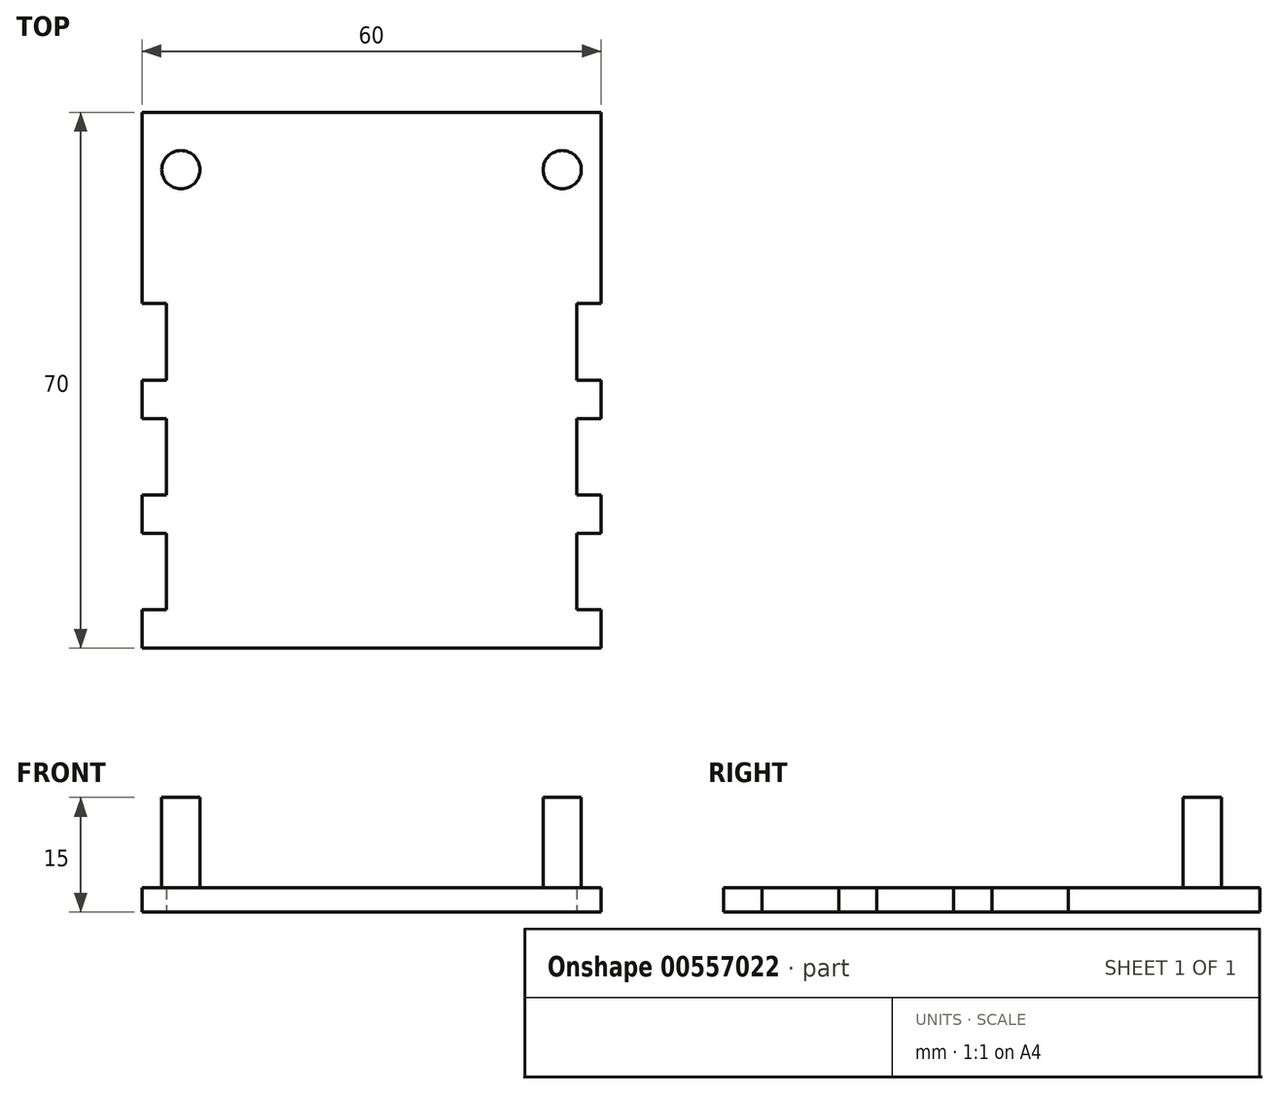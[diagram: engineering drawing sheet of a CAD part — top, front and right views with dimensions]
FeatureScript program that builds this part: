
annotation { "Feature Type Name" : "Feature", "Feature Type Description" : "" }
export const myFeature = defineFeature(function(context is Context, id is Id, definition is map)
    precondition{}
    {
        {
            var Q0;
            Q0=qCreatedBy(makeId("Top.planeOp"),FACE);
            var sketch = newSketch(context, id + "F0", { "sketchPlane" : qUnion([Q0])});
            skLineSegment(sketch, "E0.bottom", {"start": v(-25.57, 6.26) * mm, "end": v(34.43, 6.26) * mm});
            skLineSegment(sketch, "E0.top", {"start": v(-25.57, -63.74) * mm, "end": v(34.43, -63.74) * mm});
            skLineSegment(sketch, "E0.left", {"start": v(-25.57, 6.26) * mm, "end": v(-25.57, -18.74) * mm});
            skLineSegment(sketch, "E0.right", {"start": v(34.43, 6.26) * mm, "end": v(34.43, -18.74) * mm});
            skLineSegment(sketch, "E1.bottom", {"start": v(31.23, -48.74) * mm, "end": v(34.43, -48.74) * mm});
            skLineSegment(sketch, "E1.top", {"start": v(31.23, -58.74) * mm, "end": v(34.43, -58.74) * mm});
            skLineSegment(sketch, "E1.left", {"start": v(31.23, -48.74) * mm, "end": v(31.23, -58.74) * mm});
            skLineSegment(sketch, "E2.bottom", {"start": v(31.23, -33.74) * mm, "end": v(34.43, -33.74) * mm});
            skLineSegment(sketch, "E2.top", {"start": v(31.23, -43.74) * mm, "end": v(34.43, -43.74) * mm});
            skLineSegment(sketch, "E2.left", {"start": v(31.23, -33.74) * mm, "end": v(31.23, -43.74) * mm});
            skLineSegment(sketch, "E3.bottom", {"start": v(31.23, -18.74) * mm, "end": v(34.43, -18.74) * mm});
            skLineSegment(sketch, "E3.top", {"start": v(31.23, -28.74) * mm, "end": v(34.43, -28.74) * mm});
            skLineSegment(sketch, "E3.left", {"start": v(31.23, -18.74) * mm, "end": v(31.23, -28.74) * mm});
            skLineSegment(sketch, "E4.trimOffspring", {"start": v(34.43, -58.74) * mm, "end": v(34.43, -63.74) * mm});
            skLineSegment(sketch, "E5.trimOffspring", {"start": v(34.43, -43.74) * mm, "end": v(34.43, -48.74) * mm});
            skLineSegment(sketch, "E6.trimOffspring", {"start": v(34.43, -28.74) * mm, "end": v(34.43, -33.74) * mm});
            skLineSegment(sketch, "E7.bottom", {"start": v(-25.57, -48.74) * mm, "end": v(-22.37, -48.74) * mm});
            skLineSegment(sketch, "E7.top", {"start": v(-25.57, -58.74) * mm, "end": v(-22.37, -58.74) * mm});
            skLineSegment(sketch, "E7.right", {"start": v(-22.37, -48.74) * mm, "end": v(-22.37, -58.74) * mm});
            skLineSegment(sketch, "E8.bottom", {"start": v(-25.57, -43.74) * mm, "end": v(-22.37, -43.74) * mm});
            skLineSegment(sketch, "E8.top", {"start": v(-25.57, -33.74) * mm, "end": v(-22.37, -33.74) * mm});
            skLineSegment(sketch, "E8.right", {"start": v(-22.37, -43.74) * mm, "end": v(-22.37, -33.74) * mm});
            skLineSegment(sketch, "E9.bottom", {"start": v(-25.57, -28.74) * mm, "end": v(-22.37, -28.74) * mm});
            skLineSegment(sketch, "E9.top", {"start": v(-25.57, -18.74) * mm, "end": v(-22.37, -18.74) * mm});
            skLineSegment(sketch, "E9.right", {"start": v(-22.37, -28.74) * mm, "end": v(-22.37, -18.74) * mm});
            skLineSegment(sketch, "E10.trimOffspring", {"start": v(-25.57, -58.74) * mm, "end": v(-25.57, -63.74) * mm});
            skLineSegment(sketch, "E11.trimOffspring", {"start": v(-25.57, -43.74) * mm, "end": v(-25.57, -48.74) * mm});
            skLineSegment(sketch, "E12.trimOffspring", {"start": v(-25.57, -28.74) * mm, "end": v(-25.57, -33.74) * mm});
            skCircle(sketch, "E13", {"center": v(-20.47, -1.24) * mm, "radius": 2.5 * mm});
            skCircle(sketch, "E14", {"center": v(29.33, -1.24) * mm, "radius": 2.5 * mm});
            skSolve(sketch);
        }
        {
            var Q0;
            Q0=makeQuery(id+"F0.imprint","IMPRINT",FACE,{"disambiguationData":[TD([[makeQuery(id+"F0.imprint","IMPRINT",EDGE,{"derivedFrom":sQuery(id+"F0.wireOp",EDGE,"E0.bottom")}),-1.0]])]});
            extrude(context, id + "F1", {"entities" : qUnion([Q0]), "depth" : 3.2 * mm, "offsetDistance" : 25 * mm});
        }
        {
            var Q0;
            Q0=makeQuery(id+"F0.imprint","IMPRINT",FACE,{"disambiguationData":[TD([[makeQuery(id+"F0.imprint","IMPRINT",EDGE,{"derivedFrom":sQuery(id+"F0.wireOp",EDGE,"E14")}),1.0]])]});
            var Q1;
            Q1=makeQuery(id+"F0.imprint","IMPRINT",FACE,{"disambiguationData":[TD([[makeQuery(id+"F0.imprint","IMPRINT",EDGE,{"derivedFrom":sQuery(id+"F0.wireOp",EDGE,"E13")}),1.0]])]});
            extrude(context, id + "F2", {"entities" : qUnion([Q0, Q1]), "operationType" : NewBodyOperationType.ADD, "depth" : 15 * mm, "offsetDistance" : 25 * mm});
        }
    });
